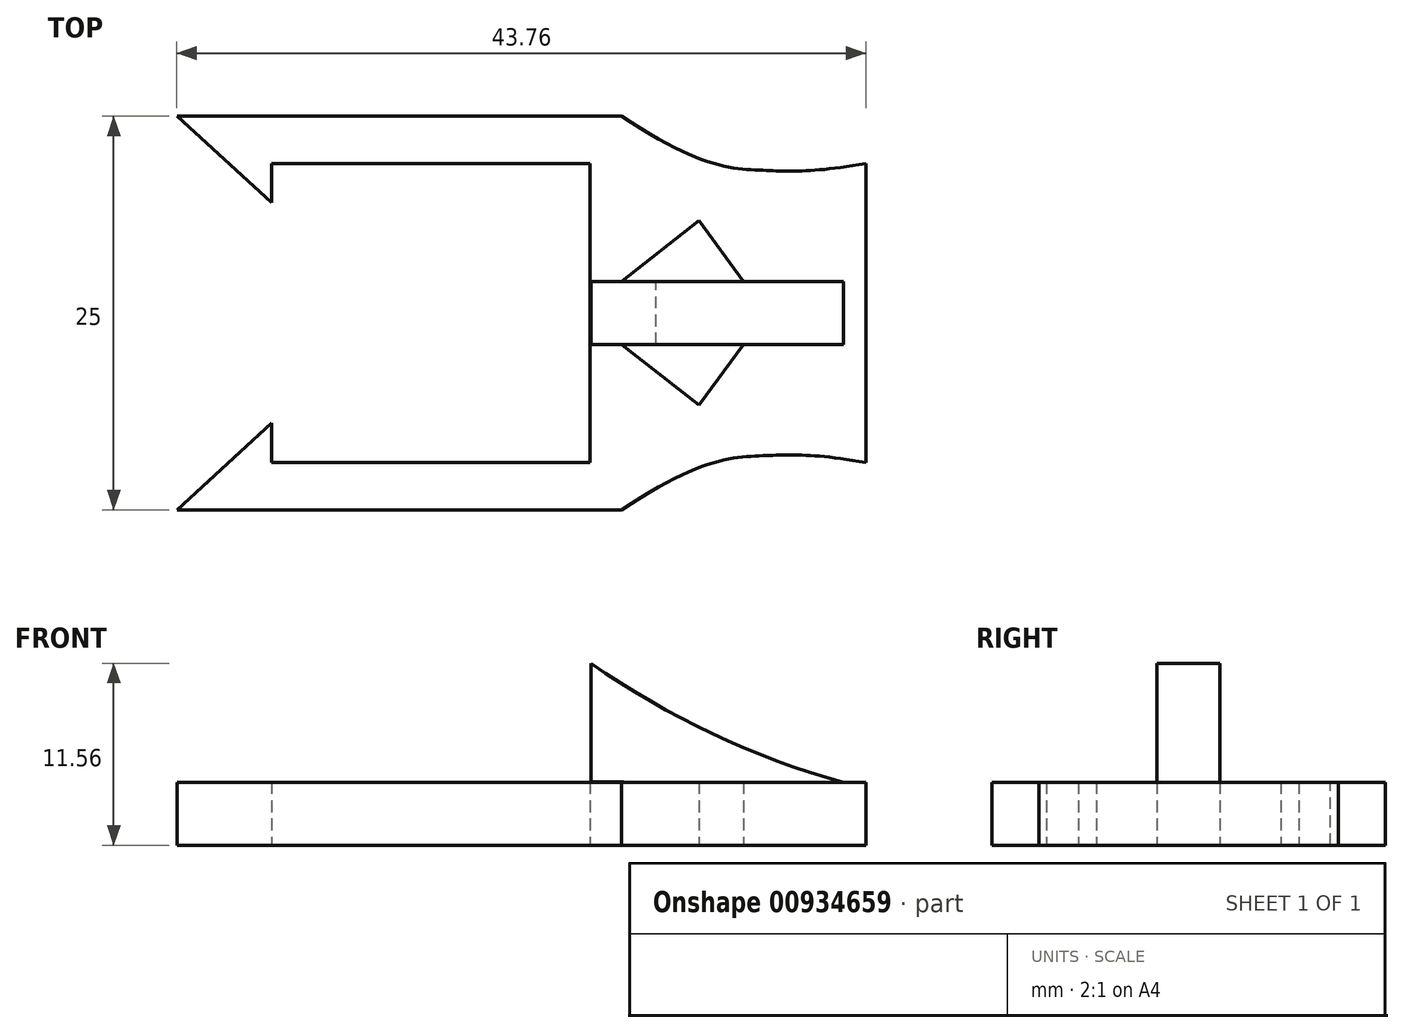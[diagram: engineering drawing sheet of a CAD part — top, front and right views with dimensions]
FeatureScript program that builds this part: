
annotation { "Feature Type Name" : "Feature", "Feature Type Description" : "" }
export const myFeature = defineFeature(function(context is Context, id is Id, definition is map)
    precondition{}
    {
        {
            var Q0;
            Q0=qCreatedBy(makeId("Top.planeOp"),FACE);
            var sketch = newSketch(context, id + "F0", { "sketchPlane" : qUnion([Q0])});
            skLineSegment(sketch, "E0.bottom", {"start": v(10.12, -9.5) * mm, "end": v(-10.13, -9.5) * mm});
            skLineSegment(sketch, "E0.top", {"start": v(10.13, 9.5) * mm, "end": v(-10.12, 9.5) * mm});
            skLineSegment(sketch, "E0.left", {"start": v(10.12, -9.5) * mm, "end": v(10.13, 9.5) * mm});
            skLineSegment(sketch, "E0.right", {"start": v(-10.12, -9.5) * mm, "end": v(-10.12, -7) * mm});
            skPoint(sketch, "E0.middle", {"position": v(0, 0) * mm});
            skLineSegment(sketch, "E1.bottom", {"start": v(12.12, -12.5) * mm, "end": v(-12.12, -12.5) * mm});
            skLineSegment(sketch, "E1.top", {"start": v(12.12, 12.5) * mm, "end": v(-12.12, 12.5) * mm});
            skLineSegment(sketch, "E1.left", {"start": v(12.12, -12.5) * mm, "end": v(12.12, 12.5) * mm});
            skLineSegment(sketch, "E2", {"start": v(-12.12, 12.5) * mm, "end": v(-16.12, 12.5) * mm});
            skLineSegment(sketch, "E3", {"start": v(-16.12, 12.5) * mm, "end": v(-10.12, 7) * mm});
            skLineSegment(sketch, "E4", {"start": v(-10.12, 7) * mm, "end": v(-10.12, 9.5) * mm});
            skLineSegment(sketch, "E5.MirrorCS", {"start": v(-16.12, -12.5) * mm, "end": v(-10.13, -7) * mm});
            skLineSegment(sketch, "E6.MirrorCS", {"start": v(-10.12, -7) * mm, "end": v(-10.12, -11) * mm});
            skLineSegment(sketch, "E7", {"start": v(-12.12, -12.5) * mm, "end": v(-16.12, -12.5) * mm});
            skLineSegment(sketch, "E8.left", {"start": v(27.62, 9.5) * mm, "end": v(27.62, -9.5) * mm});
            skFitSpline(sketch, "E9", {"points": [v(12.12, 12.5) * mm, v(21.1, 9.06) * mm, v(27.62, 9.5) * mm], "startDerivative": vector(27.3, -18.19) * mm, "endDerivative": vector(22.46, 3.99) * mm});
            skFitSpline(sketch, "E10.MirrorCS", {"points": [v(12.12, -12.5) * mm, v(21.1, -9.06) * mm, v(27.63, -9.5) * mm], "startDerivative": vector(27.3, 18.19) * mm, "endDerivative": vector(22.46, -3.99) * mm});
            skLineSegment(sketch, "E11", {"start": v(27.62, 0) * mm, "end": v(12.12, 0) * mm});
            skLineSegment(sketch, "E12.0", {"start": v(27.62, 2) * mm, "end": v(12.12, 2) * mm});
            skLineSegment(sketch, "E13.0", {"start": v(27.62, -2) * mm, "end": v(12.12, -2) * mm});
            skLineSegment(sketch, "E14", {"start": v(27.62, -9.5) * mm, "end": v(19.88, -2) * mm});
            skLineSegment(sketch, "E15", {"start": v(19.88, -2) * mm, "end": v(12.12, -12.5) * mm});
            skLineSegment(sketch, "E16", {"start": v(27.62, -2) * mm, "end": v(21.1, -9.06) * mm});
            skLineSegment(sketch, "E17", {"start": v(21.1, -9.06) * mm, "end": v(12.12, -2) * mm});
            skLineSegment(sketch, "E18", {"start": v(27.62, 9.5) * mm, "end": v(19.88, 2) * mm});
            skLineSegment(sketch, "E19", {"start": v(19.88, 2) * mm, "end": v(12.12, 12.5) * mm});
            skLineSegment(sketch, "E20", {"start": v(12.13, 2) * mm, "end": v(21.1, 9.06) * mm});
            skLineSegment(sketch, "E21", {"start": v(27.62, 2) * mm, "end": v(21.1, 9.06) * mm});
            skSolve(sketch);
        }
        {
            var Q0;
            Q0=qSketchRegion(id+"F0",true);
            extrude(context, id + "F1", {"entities" : qUnion([Q0]), "endBound" : BoundingType.SYMMETRIC, "depth" : 4 * mm, "offsetDistance" : 25 * mm});
        }
        {
            var Q0;
            Q0=qCreatedBy(makeId("Front.planeOp"),FACE);
            var sketch = newSketch(context, id + "F2", { "sketchPlane" : qUnion([Q0])});
            skLineSegment(sketch, "E22", {"start": v(10.2, 2.06) * mm, "end": v(10.2, 9.56) * mm});
            skArc(sketch, "E23", {"start": v(10.2, 9.56) * mm, "mid": v(18.2, 4.94) * mm, "end": v(26.92, 1.8) * mm});
            skLineSegment(sketch, "E24", {"start": v(10.2, 2.06) * mm, "end": v(26.92, 1.8) * mm});
            skSolve(sketch);
        }
        {
            var Q0;
            Q0=qSketchRegion(id+"F2",true);
            extrude(context, id + "F3", {"entities" : qUnion([Q0]), "operationType" : NewBodyOperationType.ADD, "endBound" : BoundingType.SYMMETRIC, "depth" : 4 * mm, "offsetDistance" : 25 * mm});
        }
    });
